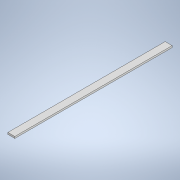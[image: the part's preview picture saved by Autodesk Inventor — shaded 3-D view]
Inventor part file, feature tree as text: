
AUTODESK INVENTOR PART (.ipt)
format: ipt  version: 2020 (Build 240168000, 168)  size: 94,720 bytes
history: native  units: in
note: dims shown in document units (in); Inventor stores cm internally (conversion verified against a paired STEP export)
features: extrude x1, sketch x1
ambient origin geometry x8: Origin, YZ Plane, XZ Plane, XY Plane, X Axis, Y Axis, Z Axis, Center Point
bodies: Solid1 (feature_tree)
feature tree (2):
  extrude  "Extrusion1"  Depth=0.5in
  sketch  "Sketch1"  dims[d0=11.293in d1=0.5in d2=0.125in d3=0.0in]
